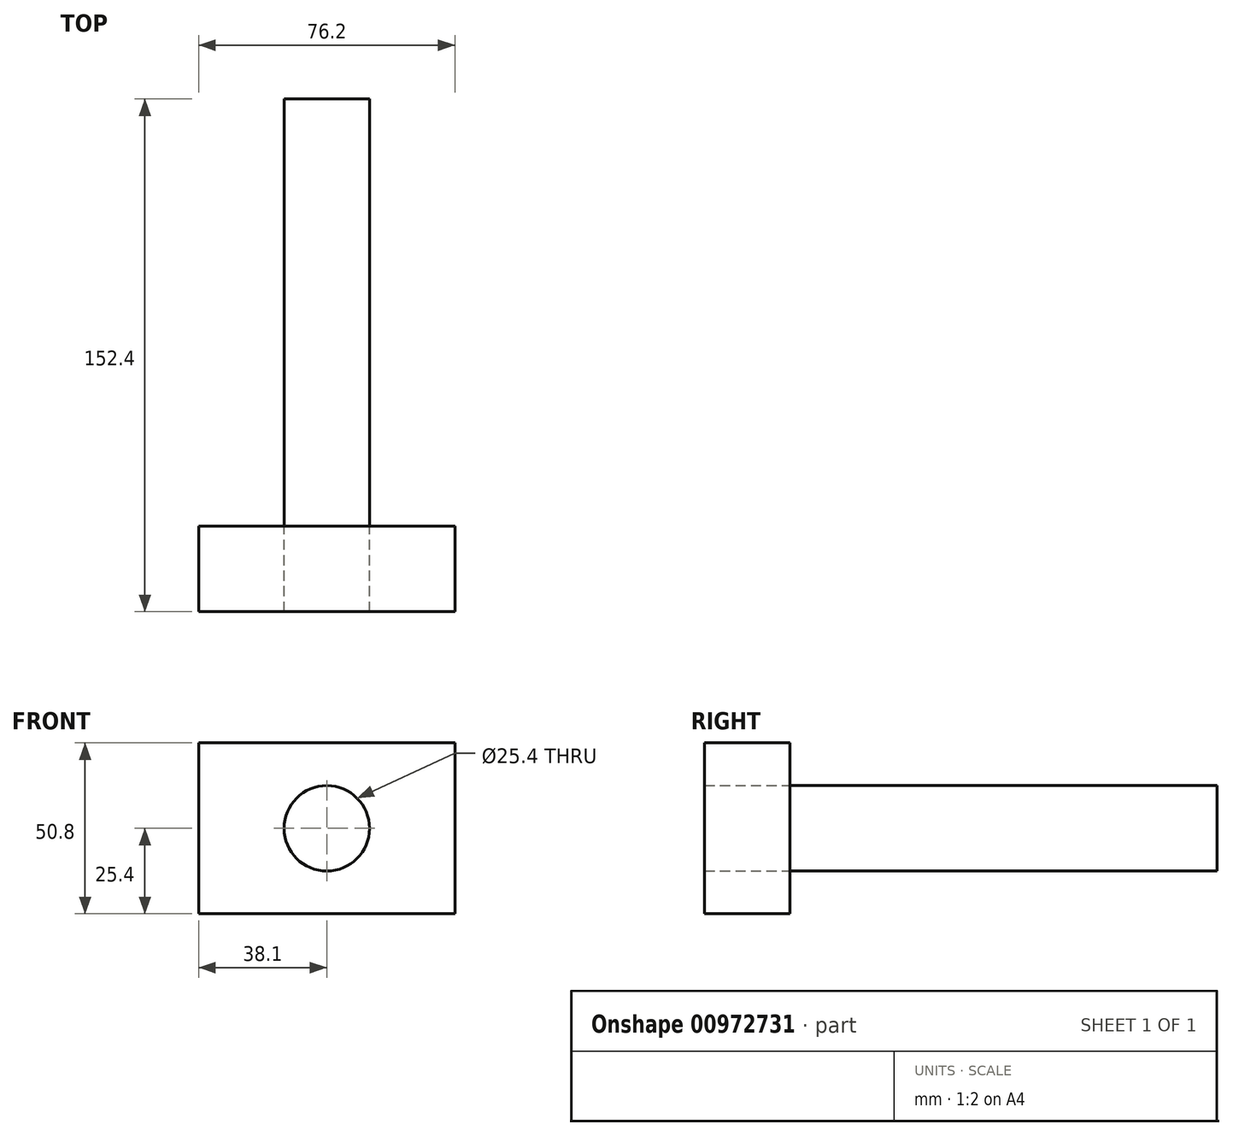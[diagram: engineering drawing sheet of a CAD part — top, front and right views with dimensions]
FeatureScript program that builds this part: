
annotation { "Feature Type Name" : "Feature", "Feature Type Description" : "" }
export const myFeature = defineFeature(function(context is Context, id is Id, definition is map)
    precondition{}
    {
        {
            var Q0;
            Q0=qCreatedBy(makeId("Front.planeOp"),FACE);
            var sketch = newSketch(context, id + "F0", { "sketchPlane" : qUnion([Q0])});
            skLineSegment(sketch, "E0.bottom", {"start": v(-38.1, 25.4) * mm, "end": v(38.1, 25.4) * mm});
            skLineSegment(sketch, "E0.top", {"start": v(-38.1, -25.4) * mm, "end": v(38.1, -25.4) * mm});
            skLineSegment(sketch, "E0.left", {"start": v(-38.1, 25.4) * mm, "end": v(-38.1, -25.4) * mm});
            skLineSegment(sketch, "E0.right", {"start": v(38.1, 25.4) * mm, "end": v(38.1, -25.4) * mm});
            skPoint(sketch, "E0.middle", {"position": v(0, 0) * mm});
            skCircle(sketch, "E1", {"center": v(0, 0) * mm, "radius": 12.7 * mm});
            skSolve(sketch);
        }
        {
            var Q0;
            Q0=makeQuery(id+"F0.imprint","IMPRINT",FACE,{"disambiguationData":[TD([[makeQuery(id+"F0.imprint","IMPRINT",EDGE,{"derivedFrom":sQuery(id+"F0.wireOp",EDGE,"E0.bottom")}),-1.0]])]});
            extrude(context, id + "F1", {"entities" : qUnion([Q0]), "depth" : 25.4 * mm, "offsetDistance" : 25.4 * mm});
        }
        {
            var Q0;
            Q0=qCreatedBy(makeId("Front.planeOp"),FACE);
            var sketch = newSketch(context, id + "F2", { "sketchPlane" : qUnion([Q0])});
            skCircle(sketch, "E2", {"center": v(0, 0) * mm, "radius": 12.7 * mm});
            skSolve(sketch);
        }
        {
            var Q0;
            Q0=makeQuery(id+"F2.imprint","IMPRINT",FACE,{"disambiguationData":[TD([[makeQuery(id+"F2.imprint","IMPRINT",EDGE,{"derivedFrom":sQuery(id+"F2.wireOp",EDGE,"E2")}),1.0]])]});
            extrude(context, id + "F3", {"entities" : qUnion([Q0]), "oppositeDirection" : true, "depth" : 127 * mm, "offsetDistance" : 25.4 * mm});
        }
    });
